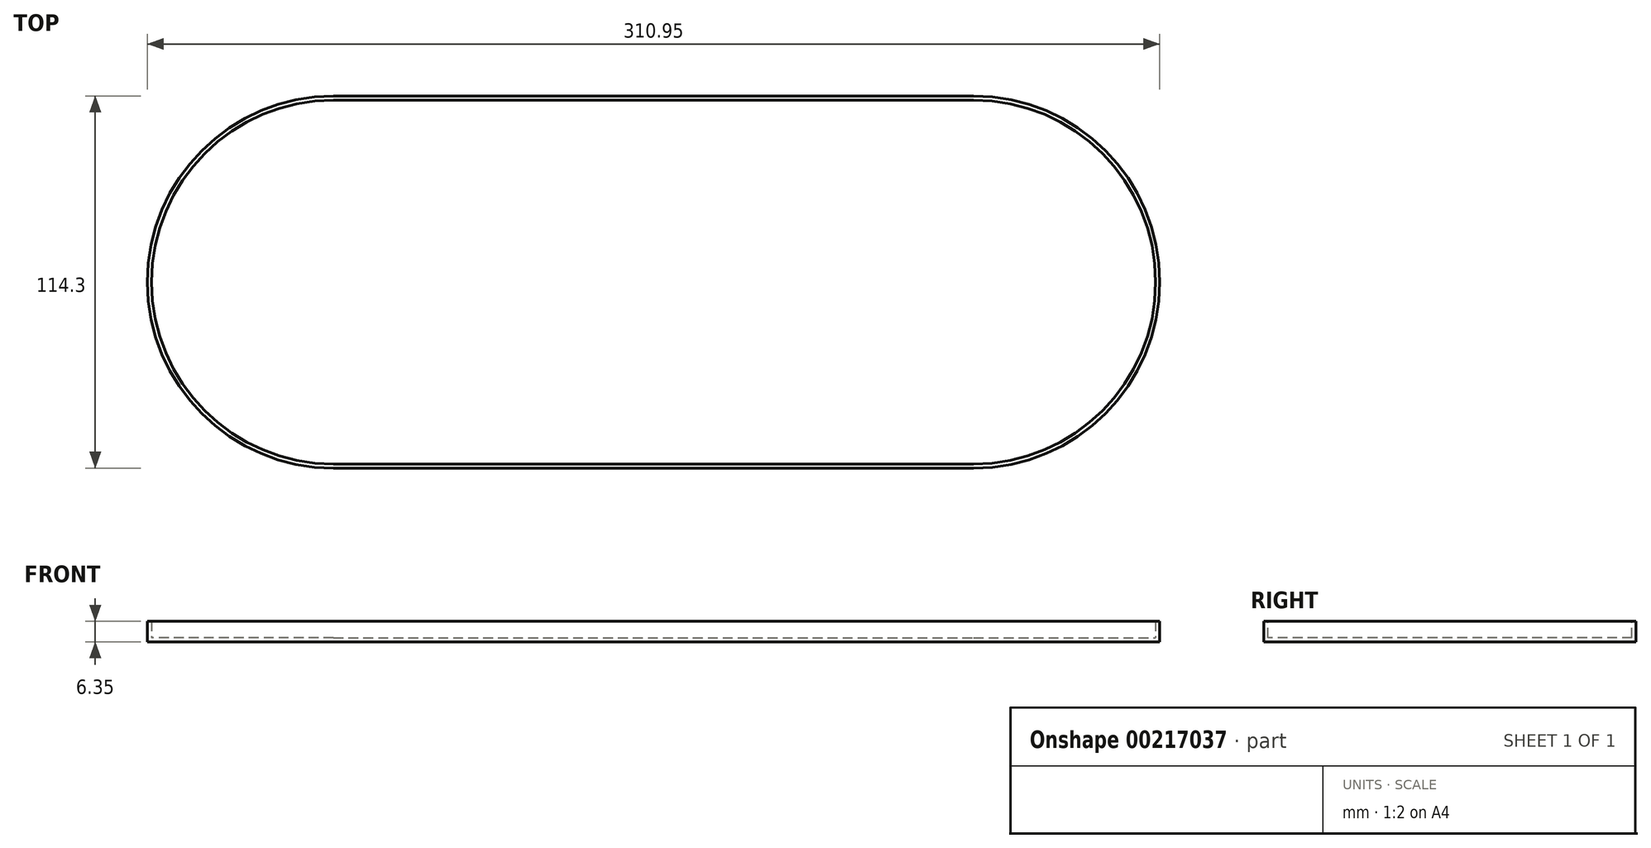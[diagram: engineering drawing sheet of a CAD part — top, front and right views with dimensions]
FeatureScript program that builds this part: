
annotation { "Feature Type Name" : "Feature", "Feature Type Description" : "" }
export const myFeature = defineFeature(function(context is Context, id is Id, definition is map)
    precondition{}
    {
        {
            var Q0;
            Q0=qCreatedBy(makeId("Top.planeOp"),FACE);
            var sketch = newSketch(context, id + "F0", { "sketchPlane" : qUnion([Q0])});
            skArc(sketch, "E0", {"start": v(-196.65, 57.15) * mm, "mid": v(-253.8, 0) * mm, "end": v(-196.65, -57.15) * mm});
            skArc(sketch, "E1", {"start": v(0, -57.15) * mm, "mid": v(57.15, 0) * mm, "end": v(0, 57.15) * mm});
            skLineSegment(sketch, "E2", {"start": v(-196.65, 57.15) * mm, "end": v(0, 57.15) * mm});
            skLineSegment(sketch, "E3", {"start": v(-196.65, -57.15) * mm, "end": v(0, -57.15) * mm});
            skSolve(sketch);
        }
        {
            var Q0;
            Q0 = qSketchRegion(id + "F0", true);
            extrude(context, id + "F1", {"entities" : qUnion([Q0]), "depth" : 6.35 * mm});
        }
        {
            var Q0;
            Q0=makeQuery(id+"F1.opExtrude","CAP_FACE",FACE,{"disambiguationData":[OSD([sQuery(id+"F0.wireOp",EDGE,"E0"),sQuery(id+"F0.wireOp",EDGE,"E1"),sQuery(id+"F0.wireOp",EDGE,"E2"),sQuery(id+"F0.wireOp",EDGE,"E3")])],"isStart":false});
            shell(context, id + "F2", {"entities" : qUnion([Q0]), "thickness" : 1.27 * mm});
        }
    });
